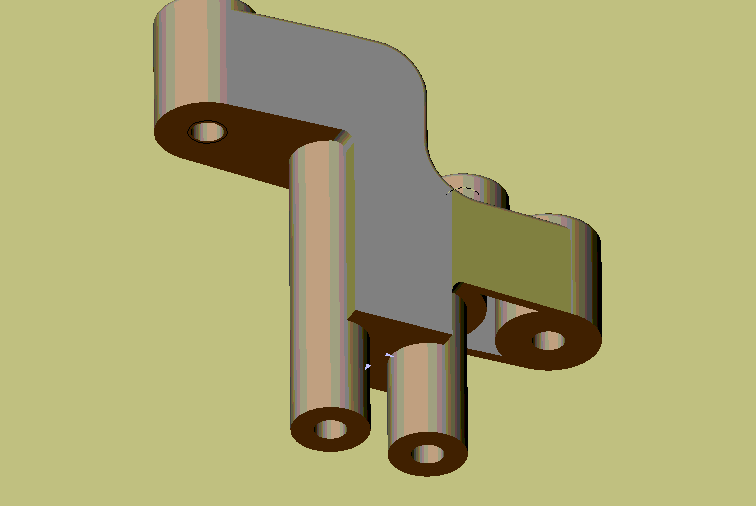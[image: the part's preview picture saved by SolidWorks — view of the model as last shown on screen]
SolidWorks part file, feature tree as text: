
SOLIDWORKS PART (.sldprt)
format: sldprt  version: not decoded by parser v0  size: 449,536 bytes
history: native  units: mm
features: sketch x20, extrude x8, fillet x6, hole x5, thread x5, plane x3, cut_extrude x2, material x1 (+8 scaffold rows collapsed)
feature tree (58):
  scaffold x8  (default folders/planes/origin — collapsed)
  material  "Matériau <non spécifié>"
  plane  "Plane1"
  plane  "Plane2"
  plane  "Plane3"
  sketch  "Esquisse1"  dims[c1.D1=6.0mm c1.D3=3.0mm c1.D2=8.0mm c2.D3=9.0mm c2.D4=4.5mm]
  extrude  "Base-Extrusion"  Depth=5mm
  sketch  "Esquisse2"  dims[D1=3.0mm D2=3.0mm]
  extrude  "Boss.-Extru.1"  Depth=8mm
  sketch  "Esquisse3"  dims[D2=8.0mm D1=14.0mm D3=0.5mm]
  extrude  "Boss.-Extru.4"  Depth=8mm
  sketch  "Esquisse4"
  extrude  "Boss.-Extru.5"  Depth=1mm
  fillet  "Congé1"  Radius=0.5mm
  sketch  "Esquisse5"
  cut_extrude  "Enlèv. mat.-Extru.1"  Depth=7mm
  sketch  "Esquisse6"  dims[D2=8.0mm D1=14.0mm D3=4.0mm]
  extrude  "Boss.-Extru.6"  Depth=12mm
  sketch  "Esquisse7"  dims[D1=9.0mm]
  cut_extrude  "Enlèv. mat.-Extru.2"  Depth=3mm
  sketch  "Esquisse8"
  extrude  "Boss.-Extru.7"  [1 undecoded]
  fillet  "Congé2"  Radius=1mm
  fillet  "Congé3"  Radius=4mm
  sketch  "Esquisse9"  dims[D1=8.0mm]
  extrude  "Boss.-Extru.8"  Depth=1mm
  fillet  "Congé4"  Radius=0.5mm
  fillet  "Congé5"  Radius=0.5mm
  hole  "Perçage1"  Diameter=2.5mm Depth=8.5mm
  sketch  "Esquisse11"
  sketch  "Esquisse10"  dims[hole-wizard template sketch: 47 standard entries collapsed; hole parameters kept: c15.Profondeur du perçage=8.5mm c15.D3=~14.816244mm c15.Angle de pointe=180.0deg]
  thread  "Représentation de filetage1"  Diameter=6mm  [1 undecoded]
  hole  "Perçage2"  Diameter=2.5mm Depth=8.5mm
  sketch  "Esquisse13"
  sketch  "Esquisse12"  dims[hole-wizard template sketch: 47 standard entries collapsed; hole parameters kept: c15.Profondeur du perçage=8.5mm c15.D3=~14.816244mm c15.Angle de pointe=180.0deg]
  thread  "Représentation de filetage2"  Diameter=6mm  [1 undecoded]
  hole  "Perçage3"  Diameter=2.5mm Depth=21mm
  sketch  "Esquisse16"
  sketch  "Esquisse15"  dims[hole-wizard template sketch: 60 standard entries collapsed; hole parameters kept: c18.Profondeur du perçage jusqu'au prochain=21.0mm]
  thread  "Représentation de filetage3"  Diameter=6mm  [1 undecoded]
  hole  "Perçage4"  Diameter=2.5mm Depth=10mm
  sketch  "Esquisse18"
  sketch  "Esquisse17"  dims[hole-wizard template sketch: 60 standard entries collapsed; hole parameters kept: c18.Profondeur du perçage jusqu'au prochain=10.0mm]
  thread  "Représentation de filetage4"  Diameter=6mm  [1 undecoded]
  sketch  "Esquisse19"  dims[D1=7.0mm D2=7.0mm]
  extrude  "Boss.-Extru.9"  Depth=3mm
  fillet  "Congé6"  Radius=0.5mm
  hole  "Perçage5"  Diameter=2.05mm Depth=7.25mm
  sketch  "Esquisse21"
  sketch  "Esquisse20"  dims[hole-wizard template sketch: 46 standard entries collapsed; hole parameters kept: c15.Diamètre du perçage=2.05mm c15.Profondeur du perçage=7.25mm c15.D3=~14.816244mm c15.Angle de pointe=180.0deg]
  thread  "Représentation de filetage5"  Diameter=5mm  [1 undecoded]
decode coverage: 37 of 46 modeling features carry decoded parameters
note: ~ marks probable driven/reference dimensions
note: 6 parameter values undecoded
summary: Diameter pulled from absorbed wizard sketch
note: suppression state not decoded; provenance and decode notes live in map.json
